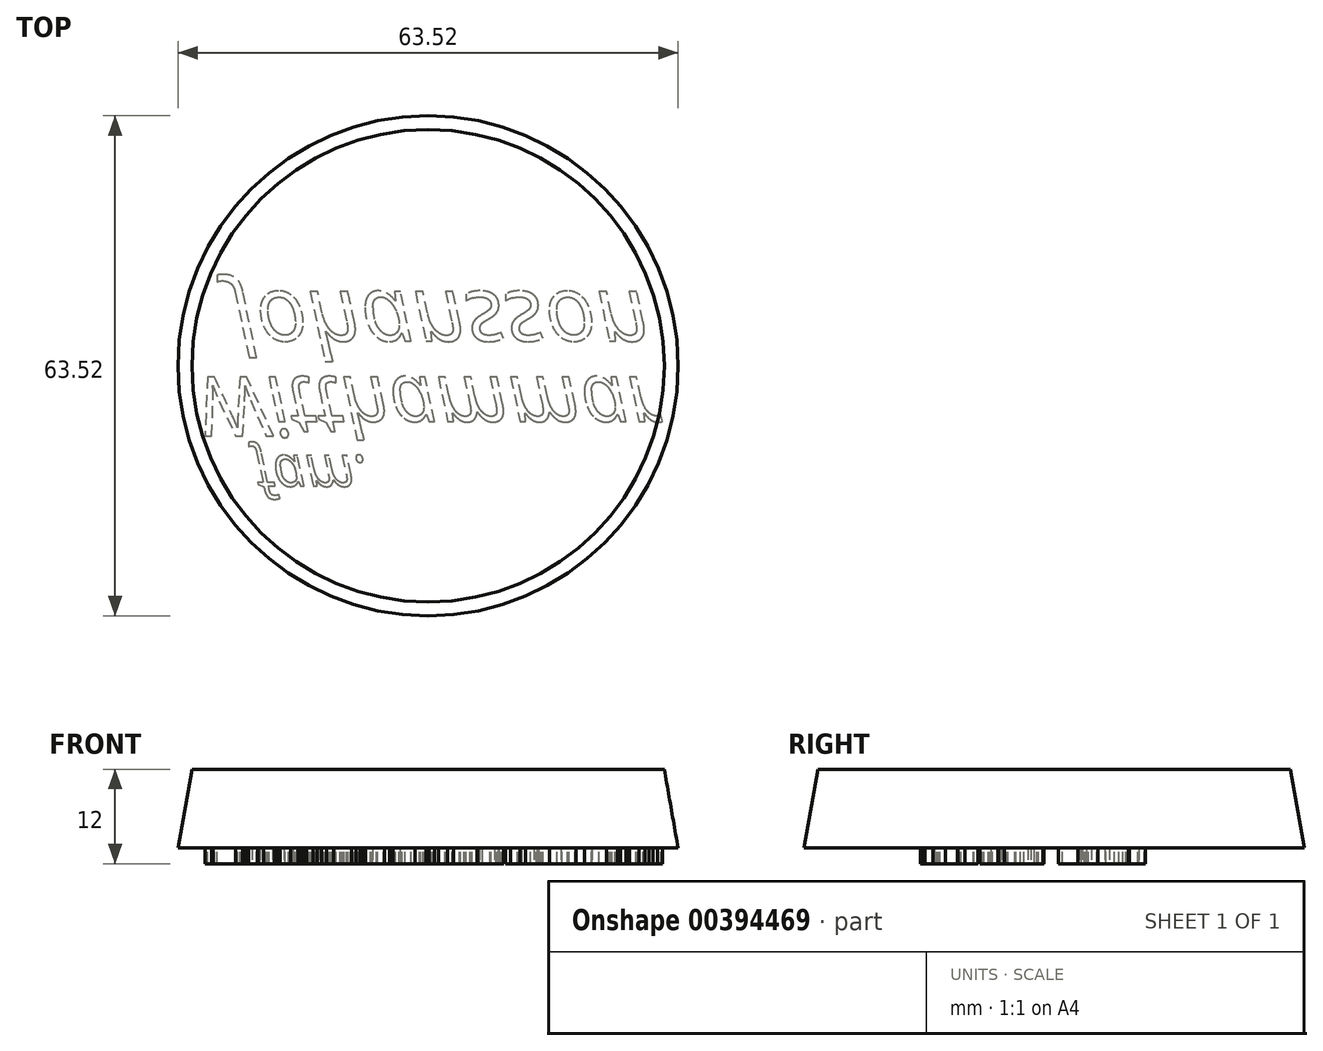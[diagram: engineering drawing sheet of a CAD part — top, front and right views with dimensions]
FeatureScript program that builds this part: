
annotation { "Feature Type Name" : "Feature", "Feature Type Description" : "" }
export const myFeature = defineFeature(function(context is Context, id is Id, definition is map)
    precondition{}
    {
        {
            var Q0;
            Q0=qCreatedBy(makeId("Top.planeOp"),FACE);
            var sketch = newSketch(context, id + "F0", { "sketchPlane" : qUnion([Q0])});
            skCircle(sketch, "E0", {"center": v(0, 0) * mm, "radius": 30 * mm});
            skSolve(sketch);
        }
        {
            var Q0;
            Q0=makeQuery(id+"F0.imprint","IMPRINT",FACE,{"disambiguationData":[TD([[makeQuery(id+"F0.imprint","IMPRINT",EDGE,{"derivedFrom":sQuery(id+"F0.wireOp",EDGE,"E0")}),1.0]])]});
            extrude(context, id + "F1", {"entities" : qUnion([Q0]), "oppositeDirection" : true, "depth" : 10 * mm, "hasDraft" : true, "draftAngle" : 10 * degree});
        }
        {
            var Q0;
            Q0=makeQuery(id+"F1.opExtrude","CAP_FACE",FACE,{"disambiguationData":[OSD([sQuery(id+"F0.wireOp",EDGE,"E0")])],"isStart":false});
            var sketch = newSketch(context, id + "F2", { "sketchPlane" : qUnion([Q0])});
            skText(sketch, "E1", { "text": "Johansson", "fontName": "OpenSans-Italic.ttf"});
            skText(sketch, "E2", { "text": "fam.", "fontName": "OpenSans-Italic.ttf"});
            skText(sketch, "E3", { "text": "Witthammar", "fontName": "OpenSans-Italic.ttf"});
            const initialGuessF2  = {"E1": [-0.025, -0.00942, 1, 0, 0.00842], "E2": [-0.022, 0.01142, 1, 0, 0.00522], "E3": [-0.0295, 0.00142, 1, 0, 0.00758]};
            skSetInitialGuess(sketch, initialGuessF2);
            skSolve(sketch);
        }
        {
            var Q0;
            Q0=qSketchRegion(id+"F2",true);
            extrude(context, id + "F3", {"entities" : qUnion([Q0]), "operationType" : NewBodyOperationType.ADD, "depth" : 2 * mm});
        }
    });
